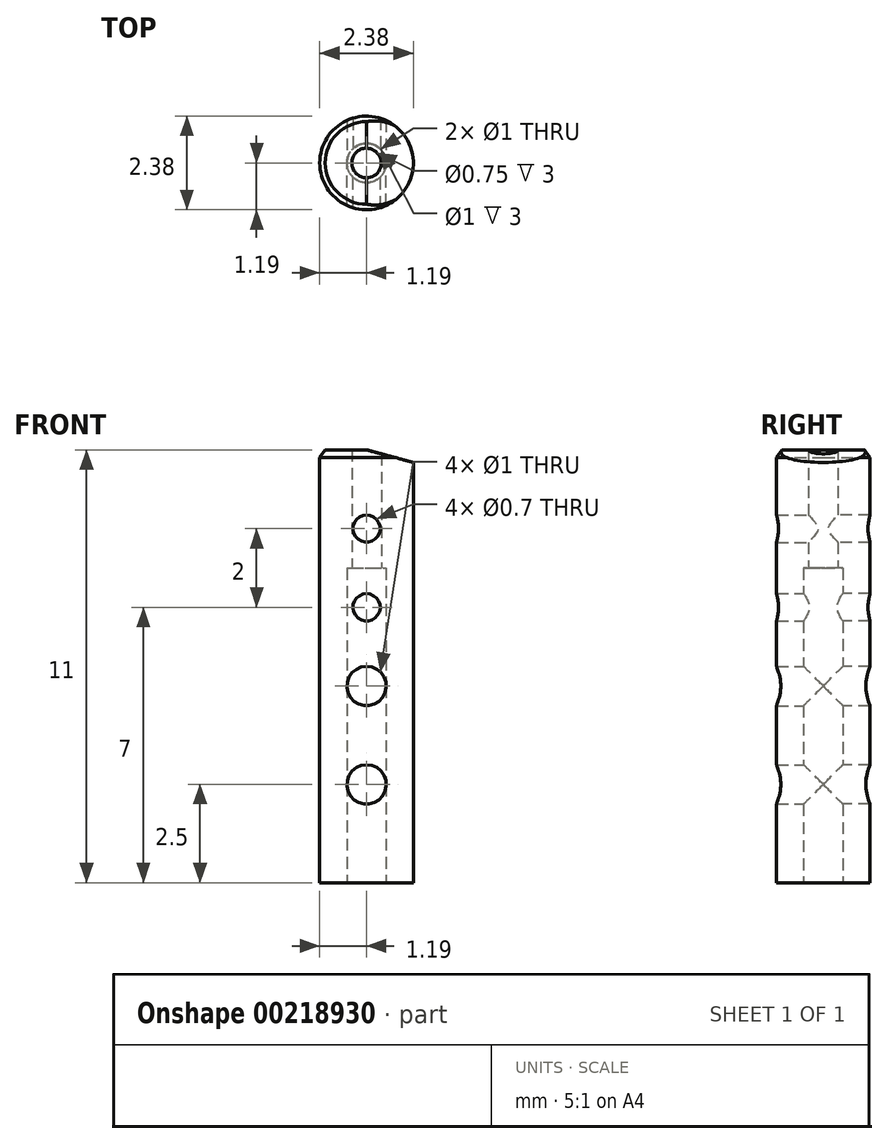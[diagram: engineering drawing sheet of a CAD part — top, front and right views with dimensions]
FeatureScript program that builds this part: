
annotation { "Feature Type Name" : "Feature", "Feature Type Description" : "" }
export const myFeature = defineFeature(function(context is Context, id is Id, definition is map)
    precondition{}
    {
        {
            var Q0;
            Q0=qCreatedBy(makeId("Right.planeOp"),FACE);
            var sketch = newSketch(context, id + "F0", { "sketchPlane" : qUnion([Q0])});
            skLineSegment(sketch, "E0", {"start": v(0, 0) * mm, "end": v(0, 11) * mm});
            skLineSegment(sketch, "E1", {"start": v(0, 11) * mm, "end": v(-1.05, 11) * mm});
            skLineSegment(sketch, "E2", {"start": v(-1.2, 10.8) * mm, "end": v(-1.19, 0) * mm});
            skLineSegment(sketch, "E3", {"start": v(-1.19, 0) * mm, "end": v(0, 0) * mm});
            skLineSegment(sketch, "E4", {"start": v(-1.05, 11) * mm, "end": v(-1.2, 10.8) * mm});
            skSolve(sketch);
        }
        {
            var Q0;
            Q0=makeQuery(id+"F0.imprint","IMPRINT",FACE,{"disambiguationData":[TD([[makeQuery(id+"F0.imprint","IMPRINT",EDGE,{"derivedFrom":sQuery(id+"F0.wireOp",EDGE,"E0")}),1.0]])]});
            var Q1;
            Q1=sQuery(id+"F0.wireOp",EDGE,"E0");
            revolve(context, id + "F1", {"entities" : qUnion([Q0]), "axis" : qUnion([Q1]), "revolveType" : RevolveType.FULL});
        }
        {
            var Q0;
            Q0=qCreatedBy(makeId("Top.planeOp"),FACE);
            var sketch = newSketch(context, id + "F2", { "sketchPlane" : qUnion([Q0])});
            skCircle(sketch, "E5", {"center": v(0, 0) * mm, "radius": 0.37 * mm});
            skSolve(sketch);
        }
        {
            var Q0;
            Q0=qSketchRegion(id+"F2",true);
            extrude(context, id + "F3", {"entities" : qUnion([Q0]), "operationType" : NewBodyOperationType.REMOVE, "depth" : 100 * mm});
        }
        {
            var Q0;
            Q0=makeQuery(id+"F1.opRevolve","SWEPT_FACE",FACE,{"disambiguationData":[OSD([sQuery(id+"F0.wireOp",EDGE,"E3")])]});
            var sketch = newSketch(context, id + "F4", { "sketchPlane" : qUnion([Q0])});
            skCircle(sketch, "E6", {"center": v(0, 0) * mm, "radius": 0.5 * mm});
            skSolve(sketch);
        }
        {
            var Q0;
            Q0=qSketchRegion(id+"F4",true);
            extrude(context, id + "F5", {"entities" : qUnion([Q0]), "operationType" : NewBodyOperationType.REMOVE, "oppositeDirection" : true, "depth" : 8 * mm});
        }
        {
            var Q0;
            Q0=qCreatedBy(makeId("Front.planeOp"),FACE);
            var sketch = newSketch(context, id + "F6", { "sketchPlane" : qUnion([Q0])});
            skCircle(sketch, "E7", {"center": v(0, 20.84) * mm, "radius": 0.71 * mm});
            skCircle(sketch, "E8", {"center": v(0, 9) * mm, "radius": 0.35 * mm});
            skCircle(sketch, "E9", {"center": v(0, 7) * mm, "radius": 0.35 * mm});
            skCircle(sketch, "E10", {"center": v(0, 5) * mm, "radius": 0.5 * mm});
            skCircle(sketch, "E11", {"center": v(0, 2.5) * mm, "radius": 0.5 * mm});
            skCircle(sketch, "E12", {"center": v(0, 12) * mm, "radius": 0.5 * mm});
            skSolve(sketch);
        }
        {
            var Q0;
            Q0=qSketchRegion(id+"F6",true);
            extrude(context, id + "F7", {"entities" : qUnion([Q0]), "operationType" : NewBodyOperationType.REMOVE, "oppositeDirection" : true, "depth" : 25 * mm});
        }
        {
            var Q0;
            Q0=qSketchRegion(id+"F6",true);
            extrude(context, id + "F8", {"entities" : qUnion([Q0]), "operationType" : NewBodyOperationType.REMOVE, "depth" : 25 * mm});
        }
        {
            var Q0;
            Q0=qCreatedBy(makeId("Front.planeOp"),FACE);
            var sketch = newSketch(context, id + "F9", { "sketchPlane" : qUnion([Q0])});
            skLineSegment(sketch, "E13", {"start": v(0, 11) * mm, "end": v(3.06, 11) * mm});
            skLineSegment(sketch, "E14", {"start": v(3.06, 11) * mm, "end": v(3.06, 10.18) * mm});
            skLineSegment(sketch, "E15", {"start": v(3.06, 10.18) * mm, "end": v(0, 11) * mm});
            skSolve(sketch);
        }
        {
            var Q0;
            Q0=qSketchRegion(id+"F9",true);
            extrude(context, id + "F10", {"entities" : qUnion([Q0]), "operationType" : NewBodyOperationType.REMOVE, "oppositeDirection" : true, "depth" : 5 * mm});
        }
        {
            var Q0;
            Q0=qSketchRegion(id+"F9",true);
            extrude(context, id + "F11", {"entities" : qUnion([Q0]), "operationType" : NewBodyOperationType.REMOVE, "depth" : 25 * mm});
        }
    });
